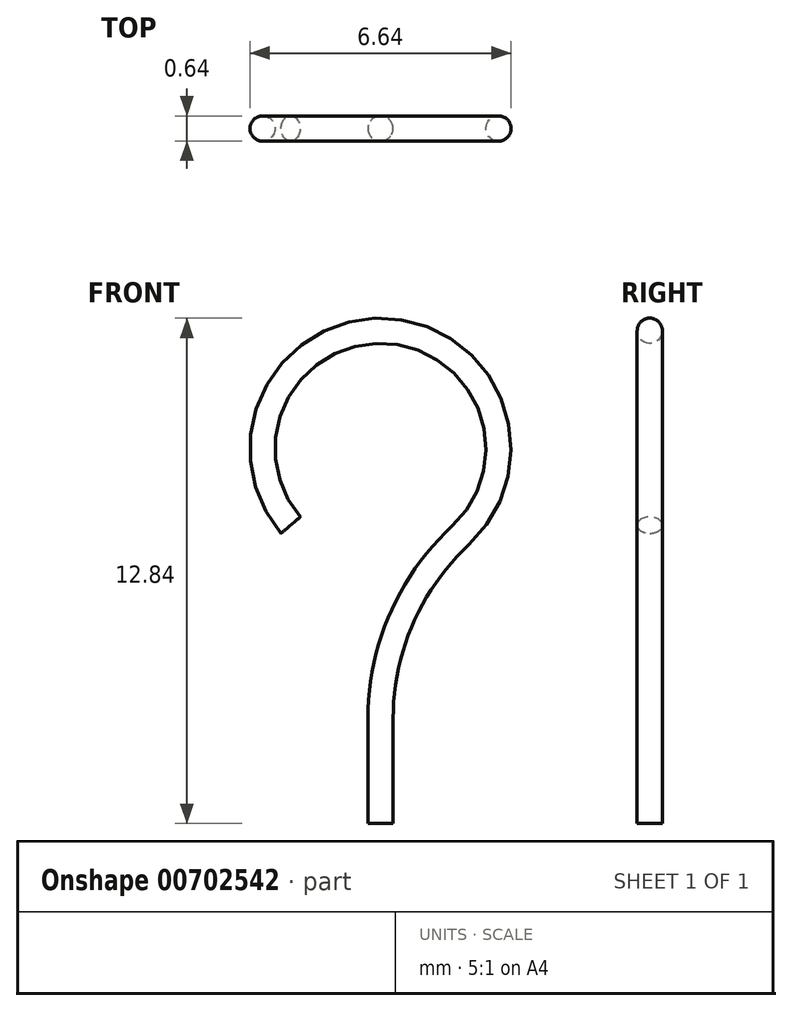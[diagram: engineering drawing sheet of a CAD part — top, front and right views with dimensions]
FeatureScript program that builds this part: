
annotation { "Feature Type Name" : "Feature", "Feature Type Description" : "" }
export const myFeature = defineFeature(function(context is Context, id is Id, definition is map)
    precondition{}
    {
        {
            var Q0;
            Q0=qCreatedBy(makeId("Front.planeOp"),FACE);
            var sketch = newSketch(context, id + "F0", { "sketchPlane" : qUnion([Q0])});
            skLineSegment(sketch, "E0", {"start": v(0, 0) * mm, "end": v(0, 6.35) * mm});
            skLineSegment(sketch, "E1", {"start": v(0, 6.35) * mm, "end": v(0, 12.7) * mm});
            skArc(sketch, "E2", {"start": v(2.04, 7.33) * mm, "mid": v(0.18, 12.52) * mm, "end": v(-2.28, 7.58) * mm});
            skLineSegment(sketch, "E3", {"start": v(0, 2.67) * mm, "end": v(0, 0) * mm});
            skArc(sketch, "E4.filletArc", {"start": v(2.04, 7.33) * mm, "mid": v(0.53, 5.2) * mm, "end": v(0, 2.67) * mm});
            skSolve(sketch);
        }
        {
            var Q0;
            Q0=qCreatedBy(makeId("Top.planeOp"),FACE);
            var sketch = newSketch(context, id + "F1", { "sketchPlane" : qUnion([Q0])});
            skCircle(sketch, "E5", {"center": v(0, 0) * mm, "radius": 0.32 * mm});
            skSolve(sketch);
        }
        {
            var Q0;
            Q0=makeQuery(id+"F1.imprint","IMPRINT",FACE,{"disambiguationData":[TD([[makeQuery(id+"F1.imprint","IMPRINT",EDGE,{"derivedFrom":sQuery(id+"F1.wireOp",EDGE,"E5")}),1.0]])]});
            var Q1;
            Q1=sQuery(id+"F0.wireOp",EDGE,"E3");
            var Q2;
            Q2=sQuery(id+"F0.wireOp",EDGE,"E4.filletArc");
            var Q3;
            Q3=sQuery(id+"F0.wireOp",EDGE,"E2");
            sweep(context, id + "F2", {"profiles" : qUnion([Q0]), "path" : qUnion([Q1, Q2, Q3])});
        }
    });
